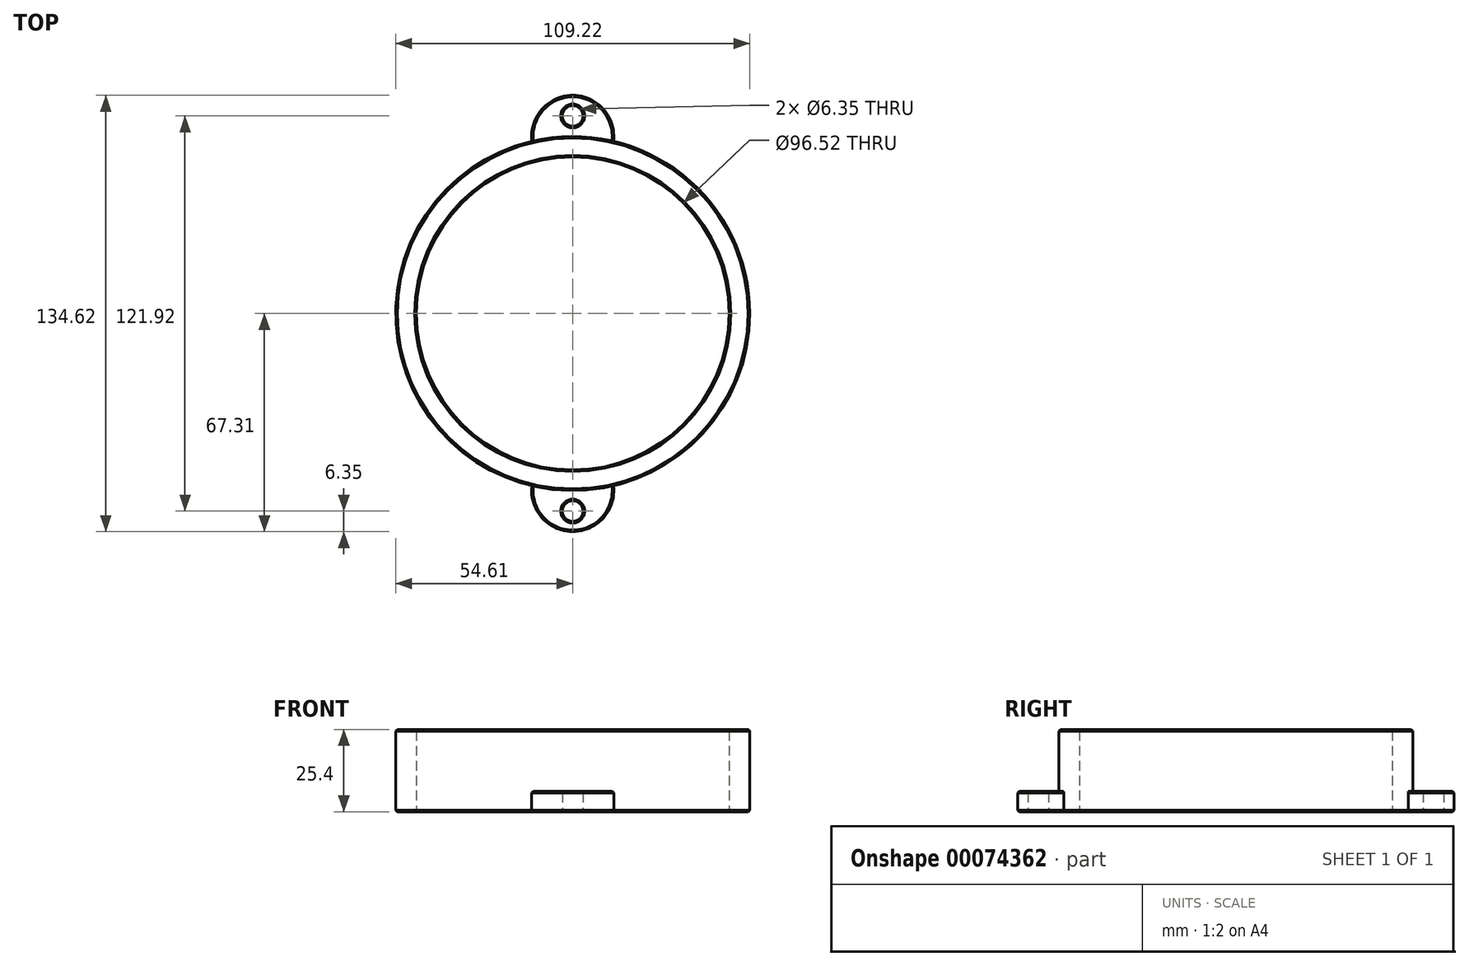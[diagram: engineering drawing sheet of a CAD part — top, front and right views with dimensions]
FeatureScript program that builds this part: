
annotation { "Feature Type Name" : "Feature", "Feature Type Description" : "" }
export const myFeature = defineFeature(function(context is Context, id is Id, definition is map)
    precondition{}
    {
        {
            var Q0;
            Q0=qCreatedBy(makeId("Top.planeOp"),FACE);
            var sketch = newSketch(context, id + "F0", { "sketchPlane" : qUnion([Q0])});
            skCircle(sketch, "E0", {"center": v(0, 0) * mm, "radius": 48.26 * mm});
            skCircle(sketch, "E1", {"center": v(0, 0) * mm, "radius": 54.61 * mm});
            skCircle(sketch, "E2", {"center": v(0, 54.61) * mm, "radius": 12.7 * mm});
            skCircle(sketch, "E3", {"center": v(0, -54.61) * mm, "radius": 12.7 * mm});
            skCircle(sketch, "E4", {"center": v(0, 60.96) * mm, "radius": 3.18 * mm});
            skLineSegment(sketch, "E5", {"start": v(0, 67.31) * mm, "end": v(0, -67.31) * mm, "construction": true});
            skCircle(sketch, "E6", {"center": v(0, -60.96) * mm, "radius": 3.18 * mm});
            skPoint(sketch, "E7", {"position": v(-10.28, 47.15) * mm});
            skPoint(sketch, "E8", {"position": v(10.28, 47.15) * mm});
            skPoint(sketch, "E9", {"position": v(-10.28, -47.15) * mm});
            skPoint(sketch, "E10", {"position": v(10.28, -47.15) * mm});
            skSolve(sketch);
        }
        {
            var Q0;
            {var subQ0=sQuery(id+"F0.wireOp",EDGE,"E2");var subQ1=sQuery(id+"F0.wireOp",EDGE,"E0");var subQ2=makeQuery(id+"F0.imprint","INTERSECT",VERTEX,{"disambiguationData":[OD(0.0)],"derivedFrom":[subQ1,subQ0]});Q0=makeQuery(id+"F0.imprint","IMPRINT",FACE,{"disambiguationData":[TD([[makeQuery(id+"F0.imprint","IMPRINT",EDGE,{"disambiguationData":[TD([[subQ2,-1.0]])],"derivedFrom":subQ1}),-1.0]])]});}
            var Q1;
            {var subQ0=sQuery(id+"F0.wireOp",EDGE,"E2");var subQ1=sQuery(id+"F0.wireOp",EDGE,"E0");var subQ2=makeQuery(id+"F0.imprint","INTERSECT",VERTEX,{"disambiguationData":[OD(1.0)],"derivedFrom":[subQ1,subQ0]});Q1=makeQuery(id+"F0.imprint","IMPRINT",FACE,{"disambiguationData":[TD([[makeQuery(id+"F0.imprint","IMPRINT",EDGE,{"disambiguationData":[TD([[subQ2,1.0]])],"derivedFrom":subQ1}),-1.0]])]});}
            var Q2;
            {var subQ0=sQuery(id+"F0.wireOp",EDGE,"E2");var subQ1=sQuery(id+"F0.wireOp",EDGE,"E0");var subQ2=makeQuery(id+"F0.imprint","INTERSECT",VERTEX,{"disambiguationData":[OD(0.0)],"derivedFrom":[subQ1,subQ0]});Q2=makeQuery(id+"F0.imprint","IMPRINT",FACE,{"disambiguationData":[TD([[makeQuery(id+"F0.imprint","IMPRINT",EDGE,{"disambiguationData":[TD([[subQ2,1.0]])],"derivedFrom":subQ1}),-1.0]])]});}
            var Q3;
            {var subQ0=sQuery(id+"F0.wireOp",EDGE,"E3");var subQ1=sQuery(id+"F0.wireOp",EDGE,"E0");var subQ2=makeQuery(id+"F0.imprint","INTERSECT",VERTEX,{"disambiguationData":[OD(0.0)],"derivedFrom":[subQ1,subQ0]});Q3=makeQuery(id+"F0.imprint","IMPRINT",FACE,{"disambiguationData":[TD([[makeQuery(id+"F0.imprint","IMPRINT",EDGE,{"disambiguationData":[TD([[subQ2,-1.0]])],"derivedFrom":subQ1}),-1.0]])]});}
            extrude(context, id + "F1", {"entities" : qUnion([Q0, Q1, Q2, Q3]), "depth" : 25.4 * mm});
        }
        {
            var Q0;
            Q0=makeQuery(id+"F0.imprint","IMPRINT",FACE,{"disambiguationData":[TD([[makeQuery(id+"F0.imprint","IMPRINT",EDGE,{"derivedFrom":sQuery(id+"F0.wireOp",EDGE,"E6")}),-1.0]])]});
            var Q1;
            Q1=makeQuery(id+"F0.imprint","IMPRINT",FACE,{"disambiguationData":[TD([[makeQuery(id+"F0.imprint","IMPRINT",EDGE,{"derivedFrom":sQuery(id+"F0.wireOp",EDGE,"E4")}),-1.0]])]});
            extrude(context, id + "F2", {"entities" : qUnion([Q0, Q1]), "operationType" : NewBodyOperationType.ADD, "depth" : 6.35 * mm});
        }
        {
            var Q0;
            Q0=makeQuery(id+"F2.boolean.opBoolean","SPLIT",EDGE,{"disambiguationData":[OD(1.0)],"derivedFrom":makeQuery(id+"F1.opExtrude","CAP_EDGE",EDGE,{"disambiguationData":[OSD([sQuery(id+"F0.wireOp",EDGE,"E1")])],"isStart":true})});
            var Q1;
            Q1=makeQuery(id+"F2.boolean.opBoolean","SPLIT",EDGE,{"disambiguationData":[OD(0.0)],"derivedFrom":makeQuery(id+"F1.opExtrude","CAP_EDGE",EDGE,{"disambiguationData":[OSD([sQuery(id+"F0.wireOp",EDGE,"E1")])],"isStart":true})});
            var Q2;
            Q2=makeQuery(id+"F1.opExtrude","CAP_EDGE",EDGE,{"disambiguationData":[OSD([sQuery(id+"F0.wireOp",EDGE,"E0")])],"isStart":true});
            var Q3;
            Q3=makeQuery(id+"F2.opExtrude","CAP_EDGE",EDGE,{"disambiguationData":[OSD([sQuery(id+"F0.wireOp",EDGE,"E2")])],"isStart":true});
            var Q4;
            Q4=makeQuery(id+"F2.opExtrude","CAP_EDGE",EDGE,{"disambiguationData":[OSD([sQuery(id+"F0.wireOp",EDGE,"E4")])],"isStart":true});
            var Q5;
            Q5=makeQuery(id+"F2.opExtrude","CAP_EDGE",EDGE,{"disambiguationData":[OSD([sQuery(id+"F0.wireOp",EDGE,"E3")])],"isStart":true});
            var Q6;
            Q6=makeQuery(id+"F2.opExtrude","CAP_EDGE",EDGE,{"disambiguationData":[OSD([sQuery(id+"F0.wireOp",EDGE,"E6")])],"isStart":true});
            var Q7;
            Q7=makeQuery(id+"F1.opExtrude","CAP_EDGE",EDGE,{"disambiguationData":[OSD([sQuery(id+"F0.wireOp",EDGE,"E1")])],"isStart":false});
            var Q8;
            Q8=makeQuery(id+"F1.opExtrude","CAP_EDGE",EDGE,{"disambiguationData":[OSD([sQuery(id+"F0.wireOp",EDGE,"E0")])],"isStart":false});
            var Q9;
            Q9=makeQuery(id+"F2.opExtrude","CAP_EDGE",EDGE,{"disambiguationData":[OSD([sQuery(id+"F0.wireOp",EDGE,"E3")])],"isStart":false});
            var Q10;
            Q10=makeQuery(id+"F2.opExtrude","CAP_EDGE",EDGE,{"disambiguationData":[OSD([sQuery(id+"F0.wireOp",EDGE,"E6")])],"isStart":false});
            var Q11;
            Q11=makeQuery(id+"F2.opExtrude","CAP_EDGE",EDGE,{"disambiguationData":[OSD([sQuery(id+"F0.wireOp",EDGE,"E4")])],"isStart":false});
            var Q12;
            Q12=makeQuery(id+"F2.opExtrude","CAP_EDGE",EDGE,{"disambiguationData":[OSD([sQuery(id+"F0.wireOp",EDGE,"E2")])],"isStart":false});
            chamfer(context, id + "F3", {"entities" : qUnion([Q0, Q1, Q2, Q3, Q4, Q5, Q6, Q7, Q8, Q9, Q10, Q11, Q12]), "width" : .5 * mm, "tangentPropagation" : true});
        }
    });
